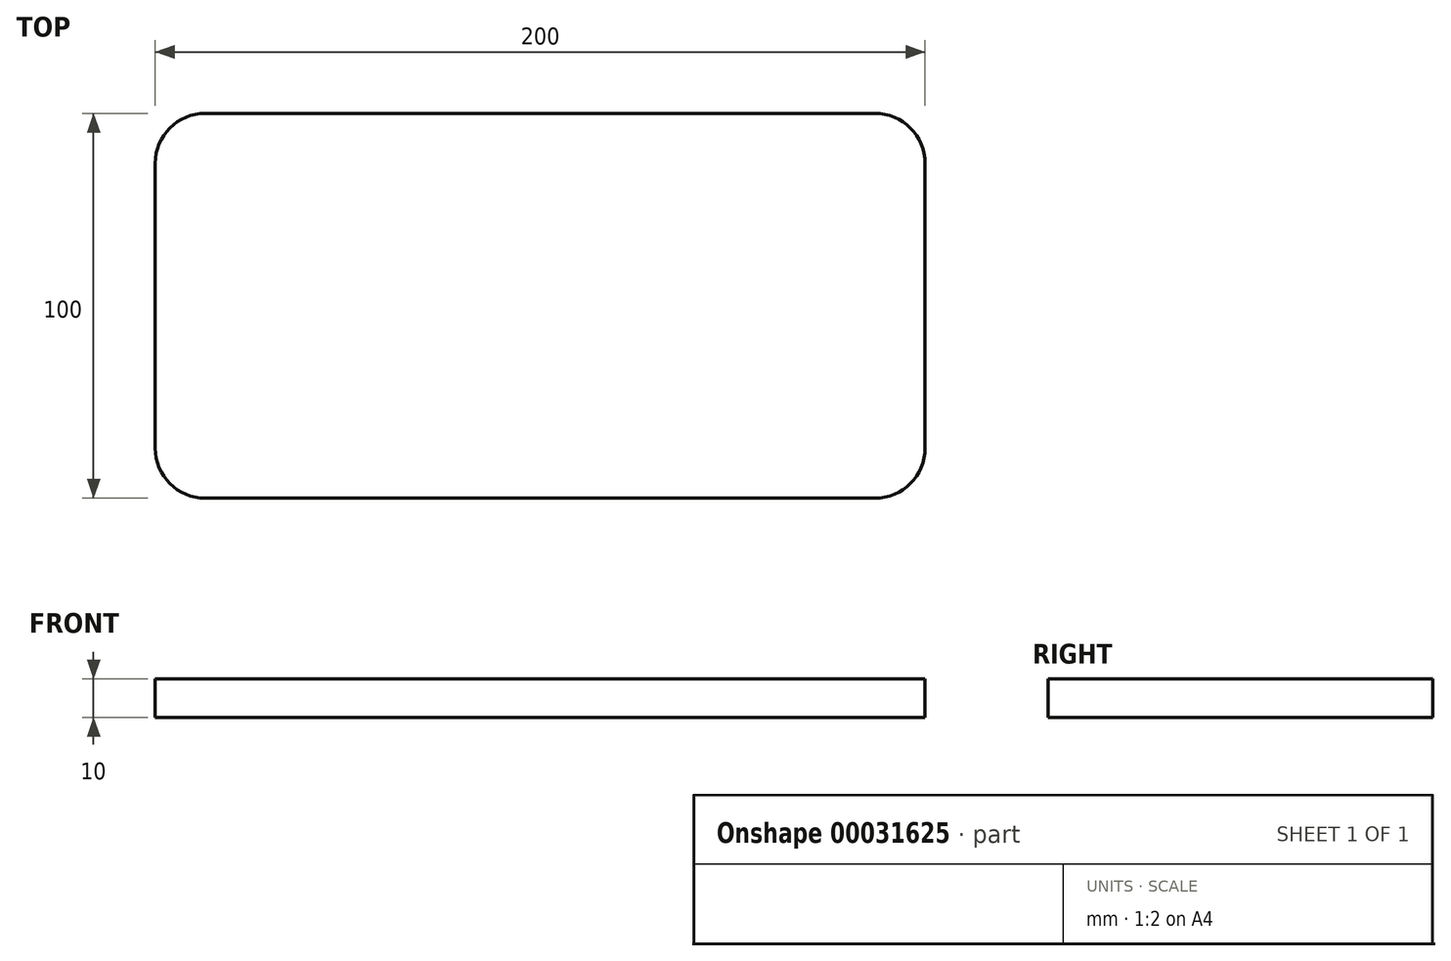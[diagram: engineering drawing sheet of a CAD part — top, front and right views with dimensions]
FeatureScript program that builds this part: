
annotation { "Feature Type Name" : "Feature", "Feature Type Description" : "" }
export const myFeature = defineFeature(function(context is Context, id is Id, definition is map)
    precondition{}
    {
        {
            var Q0;
            Q0=qCreatedBy(makeId("Top.planeOp"),FACE);
            var sketch = newSketch(context, id + "F0", { "sketchPlane" : qUnion([Q0])});
            skLineSegment(sketch, "E0.bottom", {"start": v(0, 0) * mm, "end": v(200, 0) * mm});
            skLineSegment(sketch, "E0.top", {"start": v(0, 100) * mm, "end": v(200, 100) * mm});
            skLineSegment(sketch, "E0.left", {"start": v(0, 0) * mm, "end": v(0, 100) * mm});
            skLineSegment(sketch, "E0.right", {"start": v(200, 0) * mm, "end": v(200, 100) * mm});
            skSolve(sketch);
        }
        {
            var Q0;
            Q0 = qSketchRegion(id + "F0", true);
            extrude(context, id + "F1", {"entities" : qUnion([Q0]), "depth" : 10 * mm});
        }
        {
            var Q0;
            Q0=makeQuery(id+"F1.opExtrude","SWEPT_EDGE",EDGE,{"disambiguationData":[OSD([sQuery(id+"F0.wireOp",EDGE,"E0.top"),sQuery(id+"F0.wireOp",EDGE,"E0.right")])]});
            var Q1;
            Q1=makeQuery(id+"F1.opExtrude","SWEPT_EDGE",EDGE,{"disambiguationData":[OSD([sQuery(id+"F0.wireOp",EDGE,"E0.bottom"),sQuery(id+"F0.wireOp",EDGE,"E0.right")])]});
            var Q2;
            Q2=makeQuery(id+"F1.opExtrude","SWEPT_EDGE",EDGE,{"disambiguationData":[OSD([sQuery(id+"F0.wireOp",EDGE,"E0.top"),sQuery(id+"F0.wireOp",EDGE,"E0.left")])]});
            var Q3;
            Q3=makeQuery(id+"F1.opExtrude","SWEPT_EDGE",EDGE,{"disambiguationData":[OSD([sQuery(id+"F0.wireOp",EDGE,"E0.bottom"),sQuery(id+"F0.wireOp",EDGE,"E0.left")])]});
            fillet(context, id + "F2", {"entities" : qUnion([Q0, Q1, Q2, Q3]), "radius" : 13 * mm, "tangentPropagation" : true, "allowEdgeOverflow" : false});
        }
    });
